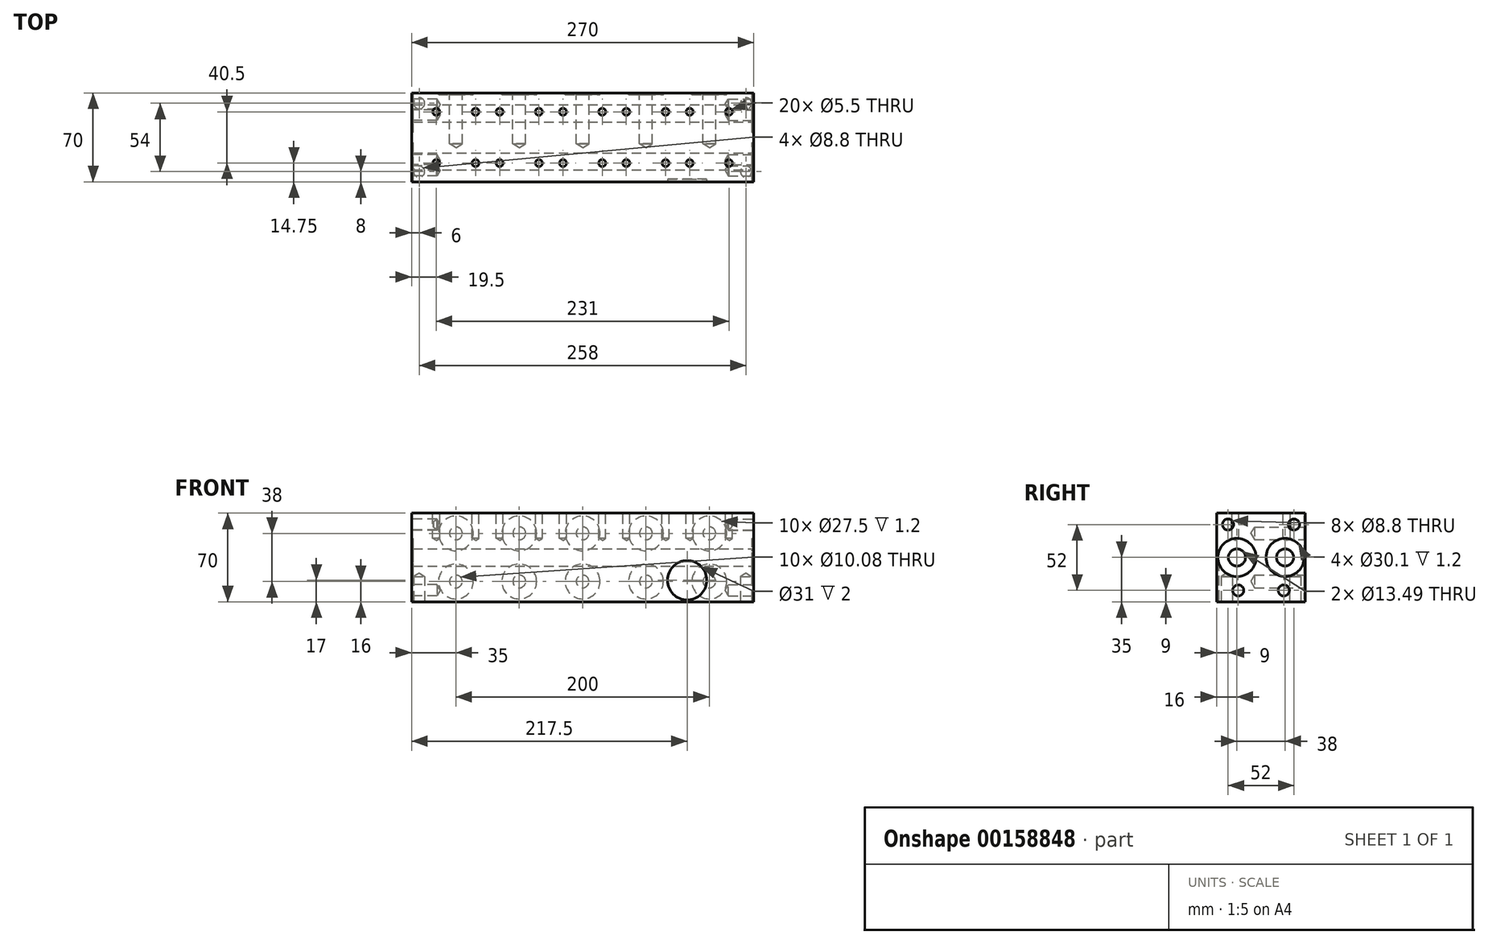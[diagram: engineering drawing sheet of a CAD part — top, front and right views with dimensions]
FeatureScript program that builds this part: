
annotation { "Feature Type Name" : "Feature", "Feature Type Description" : "" }
export const myFeature = defineFeature(function(context is Context, id is Id, definition is map)
    precondition{}
    {
        {
            var Q0;
            Q0=qCreatedBy(makeId("Right.planeOp"),FACE);
            var sketch = newSketch(context, id + "F0", { "sketchPlane" : qUnion([Q0])});
            skLineSegment(sketch, "E0.bottom", {"start": v(-35, -35) * mm, "end": v(35, -35) * mm});
            skLineSegment(sketch, "E0.top", {"start": v(-35, 35) * mm, "end": v(35, 35) * mm});
            skLineSegment(sketch, "E0.left", {"start": v(-35, -35) * mm, "end": v(-35, 35) * mm});
            skLineSegment(sketch, "E0.right", {"start": v(35, -35) * mm, "end": v(35, 35) * mm});
            skPoint(sketch, "E0.middle", {"position": v(0, 0) * mm});
            skSolve(sketch);
        }
        {
            var Q0;
            Q0=makeQuery(id+"F0.imprint","IMPRINT",FACE,{"disambiguationData":[TD([[makeQuery(id+"F0.imprint","IMPRINT",EDGE,{"derivedFrom":sQuery(id+"F0.wireOp",EDGE,"E0.bottom")}),1.0]])]});
            extrude(context, id + "F1", {"entities" : qUnion([Q0]), "depth" : 270 * mm});
        }
        {
            var Q0;
            Q0=makeQuery(id+"F1.opExtrude","CAP_FACE",FACE,{"disambiguationData":[OSD([sQuery(id+"F0.wireOp",EDGE,"E0.bottom"),sQuery(id+"F0.wireOp",EDGE,"E0.top"),sQuery(id+"F0.wireOp",EDGE,"E0.left"),sQuery(id+"F0.wireOp",EDGE,"E0.right")])],"isStart":false});
            var sketch = newSketch(context, id + "F2", { "sketchPlane" : qUnion([Q0])});
            skPoint(sketch, "E1", {"position": v(18, -26) * mm});
            skPoint(sketch, "E2", {"position": v(-18, -26) * mm});
            skPoint(sketch, "E3", {"position": v(-26, 26) * mm});
            skPoint(sketch, "E4", {"position": v(26, 25.94) * mm});
            skCircle(sketch, "E5", {"center": v(-19, 0) * mm, "radius": 15.05 * mm});
            skCircle(sketch, "E6", {"center": v(19, 0) * mm, "radius": 15.05 * mm});
            skSolve(sketch);
        }
        {
            var Q0;
            Q0=sQuery(id+"F2.wireOp",VERTEX,"E5.center");
            var Q1;
            Q1=sQuery(id+"F2.wireOp",VERTEX,"E6.center");
            var Q2;
            Q2=makeQuery(id+"F1.opExtrude","SWEPT_BODY",BODY,{"disambiguationData":[OSD([sQuery(id+"F0.wireOp",EDGE,"E0.bottom"),sQuery(id+"F0.wireOp",EDGE,"E0.top"),sQuery(id+"F0.wireOp",EDGE,"E0.left"),sQuery(id+"F0.wireOp",EDGE,"E0.right")])]});
            hole(context, id + "F3", {"style" : HoleStyle.SIMPLE, "endStyle" : HoleEndStyle.THROUGH, "standardTappedOrClearance" : lookupTablePath({ "standard" : "ANSI", "fit" : "Normal (ASME)", "size" : "1/2", "type" : "Clearance" }), "standardBlindInLast" : lookupTablePath({ "fit" : "Free", "standard" : "ANSI", "size" : "1/2", "type" : "Clearance" }), "holeDiameter" : 13.5 * mm, "locations" : qUnion([Q0, Q1]), "scope" : qUnion([Q2]), "isTappedThrough" : true});
        }
        {
            var Q0;
            Q0=sQuery(id+"F2.wireOp",VERTEX,"E3");
            var Q1;
            Q1=sQuery(id+"F2.wireOp",VERTEX,"E4");
            var Q2;
            Q2=sQuery(id+"F2.wireOp",VERTEX,"E2");
            var Q3;
            Q3=sQuery(id+"F2.wireOp",VERTEX,"E1");
            var Q4;
            Q4=makeQuery(id+"F1.opExtrude","SWEPT_BODY",BODY,{"disambiguationData":[OSD([sQuery(id+"F0.wireOp",EDGE,"E0.bottom"),sQuery(id+"F0.wireOp",EDGE,"E0.top"),sQuery(id+"F0.wireOp",EDGE,"E0.left"),sQuery(id+"F0.wireOp",EDGE,"E0.right")])]});
            hole(context, id + "F4", {"style" : HoleStyle.SIMPLE, "endStyle" : HoleEndStyle.BLIND, "standardTappedOrClearance" : lookupTablePath({ "standard" : "ISO", "fit" : "Normal", "size" : "M8", "type" : "Clearance" }), "standardBlindInLast" : lookupTablePath({ "fit" : "Standard", "standard" : "ISO", "size" : "M8", "type" : "Clearance" }), "holeDiameter" : 8.8 * mm, "holeDepth" : 20 * mm, "locations" : qUnion([Q0, Q1, Q2, Q3]), "scope" : qUnion([Q4])});
        }
        {
            var Q0;
            Q0=qSketchRegion(id+"F2",true);
            extrude(context, id + "F5", {"entities" : qUnion([Q0]), "operationType" : NewBodyOperationType.REMOVE, "oppositeDirection" : true, "depth" : 1.2 * mm});
        }
        {
            var Q0;
            Q0=makeQuery(id+"F1.opExtrude","CAP_FACE",FACE,{"disambiguationData":[OSD([sQuery(id+"F0.wireOp",EDGE,"E0.bottom"),sQuery(id+"F0.wireOp",EDGE,"E0.top"),sQuery(id+"F0.wireOp",EDGE,"E0.left"),sQuery(id+"F0.wireOp",EDGE,"E0.right")])],"isStart":true});
            var sketch = newSketch(context, id + "F6", { "sketchPlane" : qUnion([Q0])});
            skPoint(sketch, "E7", {"position": v(18, -26) * mm});
            skPoint(sketch, "E8", {"position": v(-18, -26) * mm});
            skPoint(sketch, "E9", {"position": v(-26, 25.94) * mm});
            skPoint(sketch, "E10", {"position": v(26, 26) * mm});
            skCircle(sketch, "E11", {"center": v(-19, 0) * mm, "radius": 15.05 * mm});
            skCircle(sketch, "E12", {"center": v(19, 0) * mm, "radius": 15.05 * mm});
            skSolve(sketch);
        }
        {
            var Q0;
            Q0=sQuery(id+"F6.wireOp",VERTEX,"E9");
            var Q1;
            Q1=sQuery(id+"F6.wireOp",VERTEX,"E10");
            var Q2;
            Q2=sQuery(id+"F6.wireOp",VERTEX,"E8");
            var Q3;
            Q3=sQuery(id+"F6.wireOp",VERTEX,"E7");
            var Q4;
            Q4=makeQuery(id+"F1.opExtrude","SWEPT_BODY",BODY,{"disambiguationData":[OSD([sQuery(id+"F0.wireOp",EDGE,"E0.bottom"),sQuery(id+"F0.wireOp",EDGE,"E0.top"),sQuery(id+"F0.wireOp",EDGE,"E0.left"),sQuery(id+"F0.wireOp",EDGE,"E0.right")])]});
            hole(context, id + "F7", {"style" : HoleStyle.SIMPLE, "endStyle" : HoleEndStyle.BLIND, "standardTappedOrClearance" : lookupTablePath({ "standard" : "ISO", "fit" : "Normal", "size" : "M8", "type" : "Clearance" }), "standardBlindInLast" : lookupTablePath({ "fit" : "Standard", "standard" : "ISO", "size" : "M8", "type" : "Clearance" }), "holeDiameter" : 8.8 * mm, "holeDepth" : 20 * mm, "locations" : qUnion([Q0, Q1, Q2, Q3]), "scope" : qUnion([Q4])});
        }
        {
            var Q0;
            Q0=qSketchRegion(id+"F6",true);
            extrude(context, id + "F8", {"entities" : qUnion([Q0]), "operationType" : NewBodyOperationType.REMOVE, "oppositeDirection" : true, "depth" : 1.2 * mm});
        }
        {
            var Q0;
            Q0=makeQuery(id+"F1.opExtrude","SWEPT_FACE",FACE,{"disambiguationData":[OSD([sQuery(id+"F0.wireOp",EDGE,"E0.top")])]});
            var sketch = newSketch(context, id + "F9", { "sketchPlane" : qUnion([Q0])});
            skPoint(sketch, "E13", {"position": v(19.5, 20.25) * mm});
            skPoint(sketch, "E14", {"position": v(19.5, -20.25) * mm});
            skPoint(sketch, "E15", {"position": v(50.5, -20.25) * mm});
            skPoint(sketch, "E16", {"position": v(50.5, 20.25) * mm});
            skPoint(sketch, "E17.1.0.0", {"position": v(69.5, 20.25) * mm});
            skPoint(sketch, "E17.1.0.1", {"position": v(69.5, -20.25) * mm});
            skPoint(sketch, "E17.1.0.2", {"position": v(100.5, -20.25) * mm});
            skPoint(sketch, "E17.1.0.3", {"position": v(100.5, 20.25) * mm});
            skLineSegment(sketch, "E17.direction1", {"start": v(19.5, 20.25) * mm, "end": v(69.5, 20.25) * mm, "construction": true});
            skPoint(sketch, "E18.0.2.0", {"position": v(119.5, 20.25) * mm});
            skPoint(sketch, "E18.1.2.0", {"position": v(119.5, -20.25) * mm});
            skPoint(sketch, "E18.2.2.0", {"position": v(150.5, -20.25) * mm});
            skPoint(sketch, "E18.3.2.0", {"position": v(150.5, 20.25) * mm});
            skPoint(sketch, "E18.0.3.0", {"position": v(169.5, 20.25) * mm});
            skPoint(sketch, "E18.1.3.0", {"position": v(169.5, -20.25) * mm});
            skPoint(sketch, "E18.2.3.0", {"position": v(200.5, -20.25) * mm});
            skPoint(sketch, "E18.3.3.0", {"position": v(200.5, 20.25) * mm});
            skPoint(sketch, "E18.0.4.0", {"position": v(219.5, 20.25) * mm});
            skPoint(sketch, "E18.1.4.0", {"position": v(219.5, -20.25) * mm});
            skPoint(sketch, "E18.2.4.0", {"position": v(250.5, -20.25) * mm});
            skPoint(sketch, "E18.3.4.0", {"position": v(250.5, 20.25) * mm});
            skSolve(sketch);
        }
        {
            var Q0;
            Q0=sQuery(id+"F9.wireOp",VERTEX,"E13");
            var Q1;
            Q1=sQuery(id+"F9.wireOp",VERTEX,"E14");
            var Q2;
            Q2=sQuery(id+"F9.wireOp",VERTEX,"E15");
            var Q3;
            Q3=sQuery(id+"F9.wireOp",VERTEX,"E16");
            var Q4;
            Q4=sQuery(id+"F9.wireOp",VERTEX,"E17.1.0.0");
            var Q5;
            Q5=sQuery(id+"F9.wireOp",VERTEX,"E17.1.0.1");
            var Q6;
            Q6=sQuery(id+"F9.wireOp",VERTEX,"E17.1.0.2");
            var Q7;
            Q7=sQuery(id+"F9.wireOp",VERTEX,"E17.1.0.3");
            var Q8;
            Q8=sQuery(id+"F9.wireOp",VERTEX,"E18.0.2.0");
            var Q9;
            Q9=sQuery(id+"F9.wireOp",VERTEX,"E18.1.2.0");
            var Q10;
            Q10=sQuery(id+"F9.wireOp",VERTEX,"E18.2.2.0");
            var Q11;
            Q11=sQuery(id+"F9.wireOp",VERTEX,"E18.1.3.0");
            var Q12;
            Q12=sQuery(id+"F9.wireOp",VERTEX,"E18.0.3.0");
            var Q13;
            Q13=sQuery(id+"F9.wireOp",VERTEX,"E18.3.2.0");
            var Q14;
            Q14=sQuery(id+"F9.wireOp",VERTEX,"E18.3.3.0");
            var Q15;
            Q15=sQuery(id+"F9.wireOp",VERTEX,"E18.0.4.0");
            var Q16;
            Q16=sQuery(id+"F9.wireOp",VERTEX,"E18.2.3.0");
            var Q17;
            Q17=sQuery(id+"F9.wireOp",VERTEX,"E18.1.4.0");
            var Q18;
            Q18=sQuery(id+"F9.wireOp",VERTEX,"E18.3.4.0");
            var Q19;
            Q19=sQuery(id+"F9.wireOp",VERTEX,"E18.2.4.0");
            var Q20;
            Q20=makeQuery(id+"F1.opExtrude","SWEPT_BODY",BODY,{"disambiguationData":[OSD([sQuery(id+"F0.wireOp",EDGE,"E0.bottom"),sQuery(id+"F0.wireOp",EDGE,"E0.top"),sQuery(id+"F0.wireOp",EDGE,"E0.left"),sQuery(id+"F0.wireOp",EDGE,"E0.right")])]});
            hole(context, id + "F10", {"style" : HoleStyle.SIMPLE, "endStyle" : HoleEndStyle.BLIND, "standardTappedOrClearance" : lookupTablePath({ "standard" : "ISO", "fit" : "Normal", "size" : "M5", "type" : "Clearance" }), "standardBlindInLast" : lookupTablePath({ "fit" : "Standard", "standard" : "ISO", "size" : "M5", "type" : "Clearance" }), "holeDiameter" : 5.5 * mm, "holeDepth" : 20 * mm, "locations" : qUnion([Q0, Q1, Q2, Q3, Q4, Q5, Q6, Q7, Q8, Q9, Q10, Q11, Q12, Q13, Q14, Q15, Q16, Q17, Q18, Q19]), "scope" : qUnion([Q20])});
        }
        {
            var Q0;
            Q0=makeQuery(id+"F1.opExtrude","SWEPT_FACE",FACE,{"disambiguationData":[OSD([sQuery(id+"F0.wireOp",EDGE,"E0.bottom")])]});
            var sketch = newSketch(context, id + "F11", { "sketchPlane" : qUnion([Q0])});
            skPoint(sketch, "E19", {"position": v(6, 27) * mm});
            skPoint(sketch, "E20", {"position": v(6, -27) * mm});
            skPoint(sketch, "E21", {"position": v(264, 27) * mm});
            skPoint(sketch, "E22", {"position": v(264, -27) * mm});
            skSolve(sketch);
        }
        {
            var Q0;
            Q0=sQuery(id+"F11.wireOp",VERTEX,"E19");
            var Q1;
            Q1=sQuery(id+"F11.wireOp",VERTEX,"E20");
            var Q2;
            Q2=sQuery(id+"F11.wireOp",VERTEX,"E21");
            var Q3;
            Q3=sQuery(id+"F11.wireOp",VERTEX,"E22");
            var Q4;
            Q4=makeQuery(id+"F1.opExtrude","SWEPT_BODY",BODY,{"disambiguationData":[OSD([sQuery(id+"F0.wireOp",EDGE,"E0.bottom"),sQuery(id+"F0.wireOp",EDGE,"E0.top"),sQuery(id+"F0.wireOp",EDGE,"E0.left"),sQuery(id+"F0.wireOp",EDGE,"E0.right")])]});
            hole(context, id + "F12", {"style" : HoleStyle.SIMPLE, "endStyle" : HoleEndStyle.BLIND, "standardTappedOrClearance" : lookupTablePath({ "standard" : "ISO", "fit" : "Normal", "size" : "M8", "type" : "Clearance" }), "standardBlindInLast" : lookupTablePath({ "fit" : "Standard", "standard" : "ISO", "size" : "M8", "type" : "Clearance" }), "holeDiameter" : 8.8 * mm, "holeDepth" : 20 * mm, "locations" : qUnion([Q0, Q1, Q2, Q3]), "scope" : qUnion([Q4])});
        }
        {
            var Q0;
            Q0=makeQuery(id+"F1.opExtrude","SWEPT_FACE",FACE,{"disambiguationData":[OSD([sQuery(id+"F0.wireOp",EDGE,"E0.right")])]});
            var sketch = newSketch(context, id + "F13", { "sketchPlane" : qUnion([Q0])});
            skPoint(sketch, "E23", {"position": v(-235, 19) * mm});
            skPoint(sketch, "E24", {"position": v(-235, -19) * mm});
            skPoint(sketch, "E25", {"position": v(-185, 19) * mm});
            skPoint(sketch, "E26", {"position": v(-185, -19) * mm});
            skCircle(sketch, "E27", {"center": v(-235, 19) * mm, "radius": 13.75 * mm});
            skCircle(sketch, "E28.0.1.0", {"center": v(-235, -19) * mm, "radius": 13.75 * mm});
            skCircle(sketch, "E28.1.0.0", {"center": v(-185, 19) * mm, "radius": 13.75 * mm});
            skCircle(sketch, "E28.1.1.0", {"center": v(-185, -19) * mm, "radius": 13.75 * mm});
            skLineSegment(sketch, "E28.direction1", {"start": v(-235, 19) * mm, "end": v(-185, 19) * mm, "construction": true});
            skLineSegment(sketch, "E28.direction2", {"start": v(-235, 19) * mm, "end": v(-235, -19) * mm, "construction": true});
            skCircle(sketch, "E29.0.2.0", {"center": v(-135, 19) * mm, "radius": 13.75 * mm});
            skCircle(sketch, "E29.0.2.1", {"center": v(-135, -19) * mm, "radius": 13.75 * mm});
            skCircle(sketch, "E29.0.3.0", {"center": v(-85, 19) * mm, "radius": 13.75 * mm});
            skCircle(sketch, "E29.0.3.1", {"center": v(-85, -19) * mm, "radius": 13.75 * mm});
            skCircle(sketch, "E29.0.4.0", {"center": v(-35, 19) * mm, "radius": 13.75 * mm});
            skCircle(sketch, "E29.0.4.1", {"center": v(-35, -19) * mm, "radius": 13.75 * mm});
            skSolve(sketch);
        }
        {
            var Q0;
            Q0=sQuery(id+"F13.wireOp",VERTEX,"E23");
            var Q1;
            Q1=sQuery(id+"F13.wireOp",VERTEX,"E25");
            var Q2;
            Q2=sQuery(id+"F13.wireOp",VERTEX,"E26");
            var Q3;
            Q3=sQuery(id+"F13.wireOp",VERTEX,"E24");
            var Q4;
            Q4=sQuery(id+"F13.wireOp",VERTEX,"E29.0.2.1.center");
            var Q5;
            Q5=sQuery(id+"F13.wireOp",VERTEX,"E29.0.2.0.center");
            var Q6;
            Q6=sQuery(id+"F13.wireOp",VERTEX,"E29.0.3.1.center");
            var Q7;
            Q7=sQuery(id+"F13.wireOp",VERTEX,"E29.0.3.0.center");
            var Q8;
            Q8=sQuery(id+"F13.wireOp",VERTEX,"E29.0.4.0.center");
            var Q9;
            Q9=sQuery(id+"F13.wireOp",VERTEX,"E29.0.4.1.center");
            var Q10;
            Q10=makeQuery(id+"F1.opExtrude","SWEPT_BODY",BODY,{"disambiguationData":[OSD([sQuery(id+"F0.wireOp",EDGE,"E0.bottom"),sQuery(id+"F0.wireOp",EDGE,"E0.top"),sQuery(id+"F0.wireOp",EDGE,"E0.left"),sQuery(id+"F0.wireOp",EDGE,"E0.right")])]});
            hole(context, id + "F14", {"style" : HoleStyle.SIMPLE, "endStyle" : HoleEndStyle.BLIND, "standardTappedOrClearance" : lookupTablePath({ "standard" : "ANSI", "fit" : "Normal (ASME)", "size" : "3/8", "type" : "Clearance" }), "standardBlindInLast" : lookupTablePath({ "fit" : "Free", "standard" : "ANSI", "size" : "3/8", "type" : "Clearance" }), "holeDiameter" : 10.08 * mm, "holeDepth" : 40 * mm, "locations" : qUnion([Q0, Q1, Q2, Q3, Q4, Q5, Q6, Q7, Q8, Q9]), "scope" : qUnion([Q10])});
        }
        {
            var Q0;
            Q0=qSketchRegion(id+"F13",true);
            extrude(context, id + "F15", {"entities" : qUnion([Q0]), "operationType" : NewBodyOperationType.REMOVE, "oppositeDirection" : true, "depth" : 1.2 * mm});
        }
        {
            var Q0;
            Q0=makeQuery(id+"F1.opExtrude","SWEPT_FACE",FACE,{"disambiguationData":[OSD([sQuery(id+"F0.wireOp",EDGE,"E0.left")])]});
            var sketch = newSketch(context, id + "F16", { "sketchPlane" : qUnion([Q0])});
            skCircle(sketch, "E30", {"center": v(217.5, -18) * mm, "radius": 15.5 * mm});
            skSolve(sketch);
        }
        {
            var Q0;
            Q0=qSketchRegion(id+"F16",true);
            extrude(context, id + "F17", {"entities" : qUnion([Q0]), "operationType" : NewBodyOperationType.REMOVE, "oppositeDirection" : true, "depth" : 2 * mm});
        }
    });
